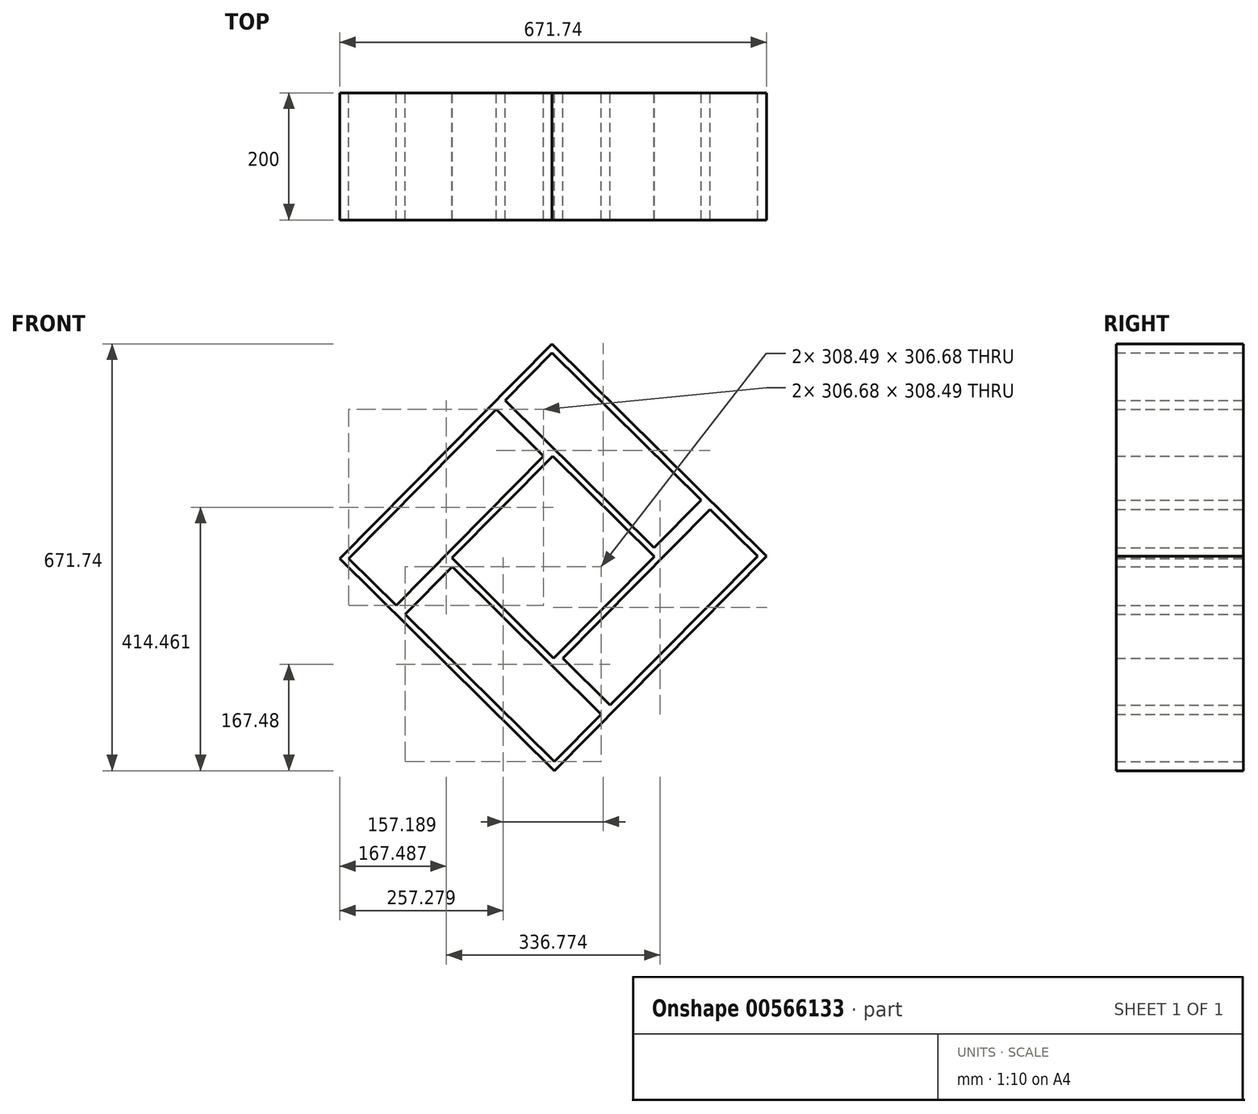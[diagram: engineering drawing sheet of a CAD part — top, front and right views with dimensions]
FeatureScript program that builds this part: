
annotation { "Feature Type Name" : "Feature", "Feature Type Description" : "" }
export const myFeature = defineFeature(function(context is Context, id is Id, definition is map)
    precondition{}
    {
        {
            var Q0;
            Q0=qCreatedBy(makeId("Front.planeOp"),FACE);
            var sketch = newSketch(context, id + "F0", { "sketchPlane" : qUnion([Q0])});
            skLineSegment(sketch, "E0", {"start": v(160, 0) * mm, "end": v(247.88, 88.89) * mm});
            skLineSegment(sketch, "E1", {"start": v(-1, 334.97) * mm, "end": v(-88.89, 246.08) * mm});
            skLineSegment(sketch, "E2", {"start": v(-88.89, 246.08) * mm, "end": v(-176.77, 157.19) * mm});
            skLineSegment(sketch, "E3", {"start": v(-176.77, 157.19) * mm, "end": v(-334.97, -2.81) * mm});
            skLineSegment(sketch, "E4", {"start": v(160, 0) * mm, "end": v(-88.89, 246.08) * mm});
            skLineSegment(sketch, "E5", {"start": v(-1, 334.97) * mm, "end": v(247.88, 88.89) * mm});
            skLineSegment(sketch, "E6", {"start": v(-334.97, -2.81) * mm, "end": v(-246.08, -90.7) * mm});
            skLineSegment(sketch, "E7", {"start": v(-246.08, -90.7) * mm, "end": v(0, 158.2) * mm});
            skLineSegment(sketch, "E8", {"start": v(-246.08, -90.7) * mm, "end": v(2.81, -336.77) * mm});
            skLineSegment(sketch, "E9", {"start": v(2.81, -336.77) * mm, "end": v(90.7, -247.88) * mm});
            skLineSegment(sketch, "E10", {"start": v(90.7, -247.88) * mm, "end": v(-158.2, -1.8) * mm});
            skLineSegment(sketch, "E11", {"start": v(160, 0) * mm, "end": v(1.8, -160) * mm});
            skLineSegment(sketch, "E12", {"start": v(90.7, -247.88) * mm, "end": v(336.77, 1) * mm});
            skLineSegment(sketch, "E13", {"start": v(336.77, 1) * mm, "end": v(247.88, 88.89) * mm});
            skLineSegment(sketch, "E14.0", {"start": v(-0.92, 320.82) * mm, "end": v(233.74, 88.8) * mm});
            skLineSegment(sketch, "E14.1", {"start": v(-0.92, 320.82) * mm, "end": v(-74.75, 246.16) * mm});
            skLineSegment(sketch, "E14.2", {"start": v(159.92, 14.14) * mm, "end": v(-74.75, 246.16) * mm});
            skLineSegment(sketch, "E14.3", {"start": v(159.92, 14.14) * mm, "end": v(233.74, 88.8) * mm});
            skLineSegment(sketch, "E15.0", {"start": v(-246.16, -76.55) * mm, "end": v(-14.14, 158.11) * mm});
            skLineSegment(sketch, "E15.1", {"start": v(-88.8, 231.94) * mm, "end": v(-14.14, 158.11) * mm});
            skLineSegment(sketch, "E15.2", {"start": v(-320.82, -2.73) * mm, "end": v(-246.16, -76.55) * mm});
            skLineSegment(sketch, "E15.3", {"start": v(-169.66, 150.16) * mm, "end": v(-320.82, -2.73) * mm});
            skLineSegment(sketch, "E15.4", {"start": v(-88.8, 231.94) * mm, "end": v(-169.66, 150.16) * mm});
            skLineSegment(sketch, "E16", {"start": v(-158.2, -1.8) * mm, "end": v(-246.08, -90.7) * mm});
            skLineSegment(sketch, "E17.0", {"start": v(-231.94, -90.62) * mm, "end": v(2.73, -322.63) * mm});
            skLineSegment(sketch, "E17.1", {"start": v(-158.11, -15.95) * mm, "end": v(-231.94, -90.62) * mm});
            skLineSegment(sketch, "E17.2", {"start": v(76.55, -247.97) * mm, "end": v(-158.11, -15.95) * mm});
            skLineSegment(sketch, "E17.3", {"start": v(2.73, -322.63) * mm, "end": v(76.55, -247.97) * mm});
            skLineSegment(sketch, "E18", {"start": v(1.8, -160) * mm, "end": v(90.7, -247.88) * mm});
            skLineSegment(sketch, "E19.0", {"start": v(167.11, -7.03) * mm, "end": v(15.95, -159.92) * mm});
            skLineSegment(sketch, "E19.1", {"start": v(167.11, -7.03) * mm, "end": v(247.97, 74.75) * mm});
            skLineSegment(sketch, "E19.2", {"start": v(322.63, 0.92) * mm, "end": v(247.97, 74.75) * mm});
            skLineSegment(sketch, "E19.3", {"start": v(90.62, -233.74) * mm, "end": v(322.63, 0.92) * mm});
            skLineSegment(sketch, "E20.0", {"start": v(15.95, -159.92) * mm, "end": v(90.62, -233.74) * mm});
            skSolve(sketch);
        }
        {
            var Q0;
            Q0=qSketchRegion(id+"F0",true);
            extrude(context, id + "F1", {"entities" : qUnion([Q0]), "depth" : 200 * mm, "offsetDistance" : 25 * mm});
        }
    });
